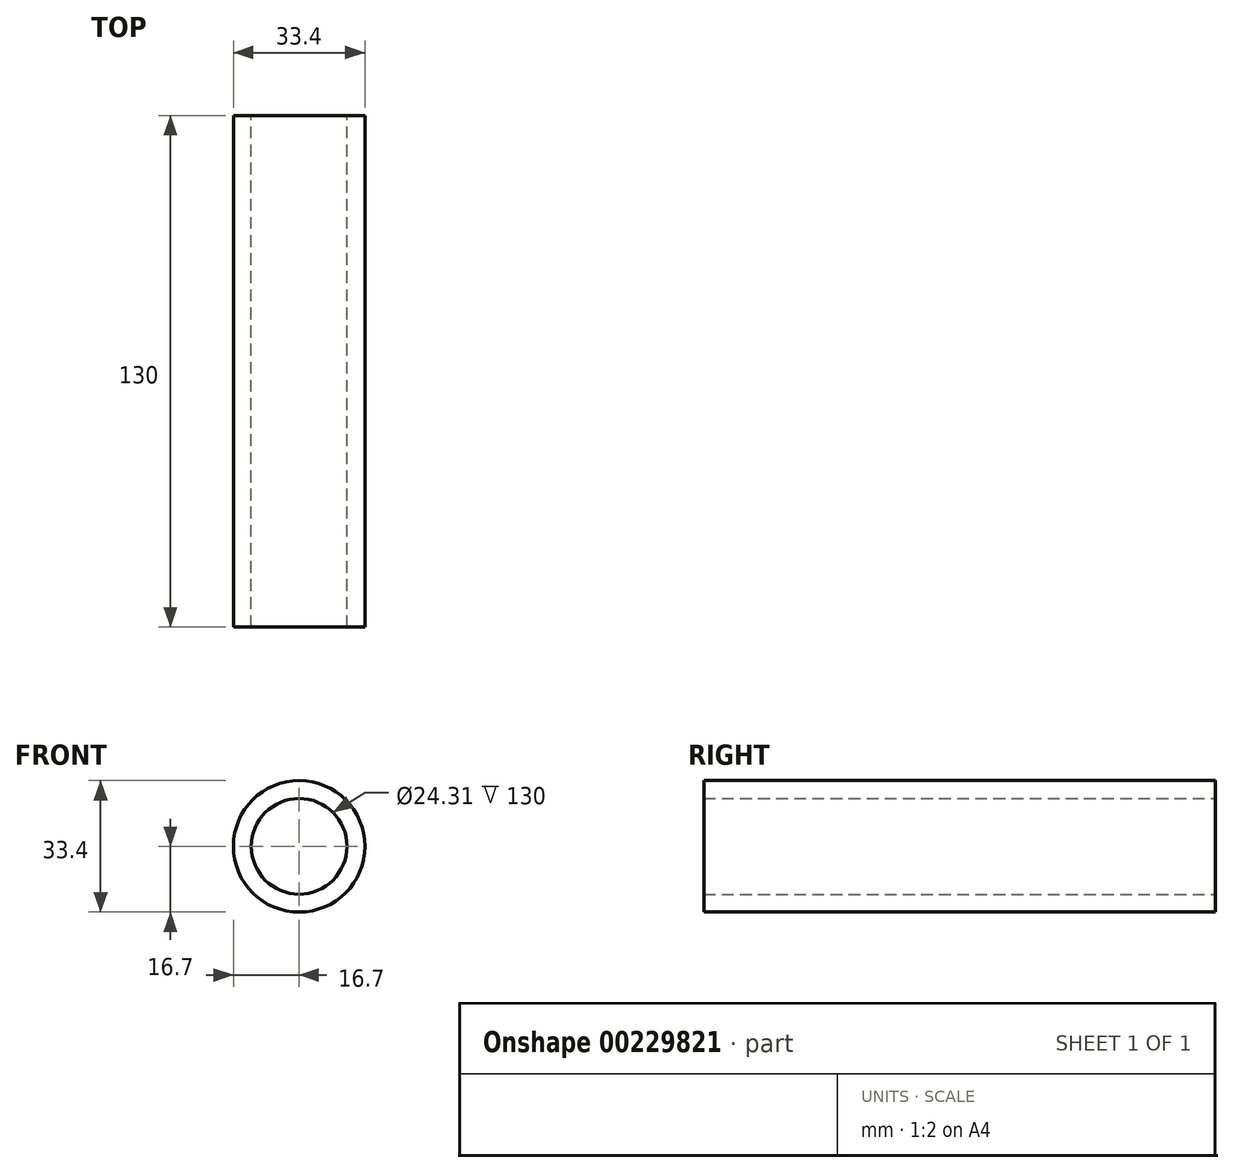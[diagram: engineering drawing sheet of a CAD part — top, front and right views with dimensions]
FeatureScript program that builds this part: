
annotation { "Feature Type Name" : "Feature", "Feature Type Description" : "" }
export const myFeature = defineFeature(function(context is Context, id is Id, definition is map)
    precondition{}
    {
        {
            var Q0;
            Q0=qCreatedBy(makeId("Front.planeOp"),FACE);
            var sketch = newSketch(context, id + "F0", { "sketchPlane" : qUnion([Q0])});
            skCircle(sketch, "E0", {"center": v(0, 0) * mm, "radius": 16.7 * mm});
            skCircle(sketch, "E1", {"center": v(0, 0) * mm, "radius": 12.15 * mm});
            skSolve(sketch);
        }
        {
            var Q0;
            Q0 = qSketchRegion(id + "F0", true);
            extrude(context, id + "F1", {"entities" : qUnion([Q0]), "depth" : 130 * mm});
        }
    });
